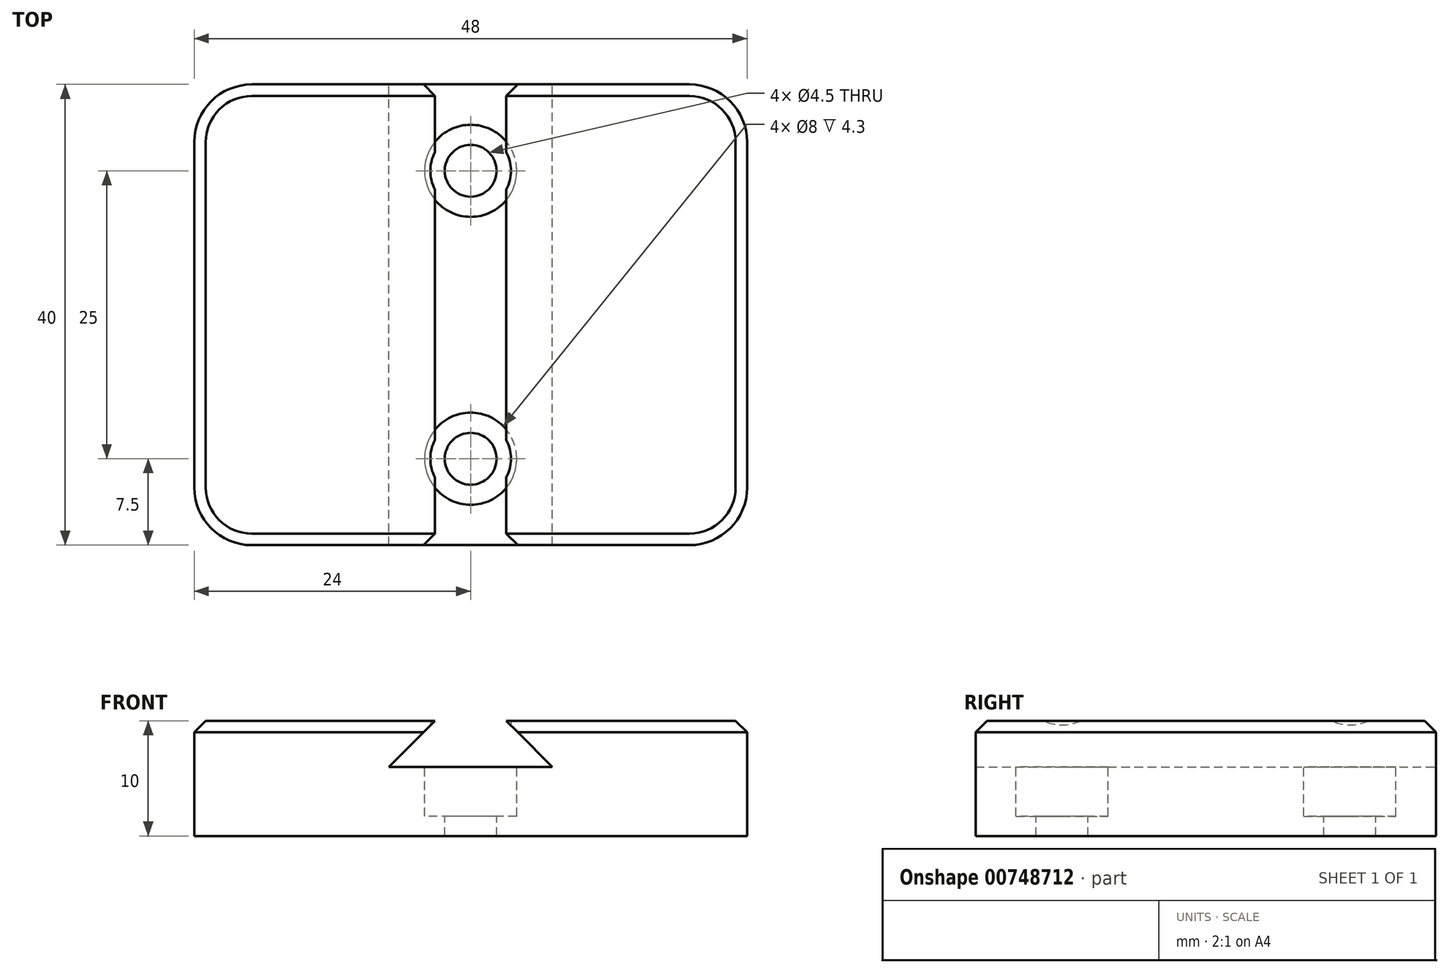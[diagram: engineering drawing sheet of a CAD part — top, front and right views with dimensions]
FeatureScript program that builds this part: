
annotation { "Feature Type Name" : "Feature", "Feature Type Description" : "" }
export const myFeature = defineFeature(function(context is Context, id is Id, definition is map)
    precondition{}
    {
        {
            var Q0;
            Q0=qCreatedBy(makeId("Front.planeOp"),FACE);
            var sketch = newSketch(context, id + "F0", { "sketchPlane" : qUnion([Q0])});
            skLineSegment(sketch, "E0", {"start": v(-24, 0) * mm, "end": v(-24, -6) * mm});
            skLineSegment(sketch, "E1", {"start": v(-24, -6) * mm, "end": v(24, -6) * mm});
            skLineSegment(sketch, "E2", {"start": v(24, -6) * mm, "end": v(24, 0) * mm});
            skLineSegment(sketch, "E3", {"start": v(-24, 0) * mm, "end": v(-24, 4) * mm});
            skLineSegment(sketch, "E4", {"start": v(-24, 4) * mm, "end": v(-3.1, 4) * mm});
            skLineSegment(sketch, "E5", {"start": v(-3.1, 4) * mm, "end": v(-7.1, 0) * mm});
            skLineSegment(sketch, "E6", {"start": v(-7.1, 0) * mm, "end": v(7.1, 0) * mm});
            skLineSegment(sketch, "E7", {"start": v(7.1, 0) * mm, "end": v(3.1, 4) * mm});
            skLineSegment(sketch, "E8", {"start": v(3.1, 4) * mm, "end": v(24, 4) * mm});
            skLineSegment(sketch, "E9", {"start": v(24, 4) * mm, "end": v(24, 0) * mm});
            skSolve(sketch);
        }
        {
            var Q0;
            Q0=makeQuery(id+"F0.imprint","IMPRINT",FACE,{"disambiguationData":[TD([[makeQuery(id+"F0.imprint","IMPRINT",EDGE,{"derivedFrom":sQuery(id+"F0.wireOp",EDGE,"E0")}),1.0]])]});
            extrude(context, id + "F1", {"entities" : qUnion([Q0]), "endBound" : BoundingType.SYMMETRIC, "depth" : 40 * mm, "offsetDistance" : 25 * mm});
        }
        {
            var Q0;
            Q0=makeQuery(id+"F1.opExtrude","CAP_EDGE",EDGE,{"disambiguationData":[OSD([sQuery(id+"F0.wireOp",EDGE,"E0"),sQuery(id+"F0.wireOp",EDGE,"E3")])],"isStart":true});
            var Q1;
            Q1=makeQuery(id+"F1.opExtrude","CAP_EDGE",EDGE,{"disambiguationData":[OSD([sQuery(id+"F0.wireOp",EDGE,"E2"),sQuery(id+"F0.wireOp",EDGE,"E9")])],"isStart":true});
            var Q2;
            Q2=makeQuery(id+"F1.opExtrude","CAP_EDGE",EDGE,{"disambiguationData":[OSD([sQuery(id+"F0.wireOp",EDGE,"E2"),sQuery(id+"F0.wireOp",EDGE,"E9")])],"isStart":false});
            var Q3;
            Q3=makeQuery(id+"F1.opExtrude","CAP_EDGE",EDGE,{"disambiguationData":[OSD([sQuery(id+"F0.wireOp",EDGE,"E0"),sQuery(id+"F0.wireOp",EDGE,"E3")])],"isStart":false});
            fillet(context, id + "F2", {"entities" : qUnion([Q0, Q1, Q2, Q3]), "radius" : 5 * mm, "tangentPropagation" : true, "allowEdgeOverflow" : false});
        }
        {
            var Q0;
            Q0=makeQuery(id+"F2.opFillet","BLEND_EDGE",EDGE,{"blendedFrom":[makeQuery(id+"F1.opExtrude","CAP_EDGE",EDGE,{"disambiguationData":[OSD([sQuery(id+"F0.wireOp",EDGE,"E0"),sQuery(id+"F0.wireOp",EDGE,"E3")])],"isStart":false}),makeQuery(id+"F1.opExtrude","SWEPT_FACE",FACE,{"disambiguationData":[OSD([sQuery(id+"F0.wireOp",EDGE,"E4")])]})],"blendedInto":[makeQuery(id+"F1.opExtrude","SWEPT_FACE",FACE,{"disambiguationData":[OSD([sQuery(id+"F0.wireOp",EDGE,"E4")])]})]});
            var Q1;
            Q1=makeQuery(id+"F1.opExtrude","CAP_EDGE",EDGE,{"disambiguationData":[OSD([sQuery(id+"F0.wireOp",EDGE,"E8")])],"isStart":false});
            chamfer(context, id + "F3", {"entities" : qUnion([Q0, Q1]), "width" : 1 * mm, "tangentPropagation" : true});
        }
        {
            var Q0;
            Q0=makeQuery(id+"F1.opExtrude","SWEPT_FACE",FACE,{"disambiguationData":[OSD([sQuery(id+"F0.wireOp",EDGE,"E6")])]});
            var sketch = newSketch(context, id + "F4", { "sketchPlane" : qUnion([Q0])});
            skPoint(sketch, "E10", {"position": v(0, 12.5) * mm});
            skPoint(sketch, "E11", {"position": v(0, -12.5) * mm});
            skCircle(sketch, "E12", {"center": v(0, -12.5) * mm, "radius": 3.5 * mm});
            skCircle(sketch, "E13", {"center": v(0, 12.5) * mm, "radius": 3.5 * mm});
            skSolve(sketch);
        }
        {
            var Q0;
            Q0=sQuery(id+"F4.wireOp",VERTEX,"E10");
            var Q1;
            Q1=sQuery(id+"F4.wireOp",VERTEX,"E11");
            var Q2;
            Q2=makeQuery(id+"F1.opExtrude","SWEPT_BODY",BODY,{"disambiguationData":[OSD([sQuery(id+"F0.wireOp",EDGE,"E0"),sQuery(id+"F0.wireOp",EDGE,"E1"),sQuery(id+"F0.wireOp",EDGE,"E2"),sQuery(id+"F0.wireOp",EDGE,"E3"),sQuery(id+"F0.wireOp",EDGE,"E4"),sQuery(id+"F0.wireOp",EDGE,"E5"),sQuery(id+"F0.wireOp",EDGE,"E6"),sQuery(id+"F0.wireOp",EDGE,"E7"),sQuery(id+"F0.wireOp",EDGE,"E8"),sQuery(id+"F0.wireOp",EDGE,"E9")])]});
            hole(context, id + "F5", {"style" : HoleStyle.C_BORE, "endStyle" : HoleEndStyle.BLIND, "holeDiameter" : 4.5 * mm, "cBoreDiameter" : 8 * mm, "cBoreDepth" : 4.3 * mm, "majorDiameter" : 5 * mm, "holeDepth" : 7 * mm, "isTappedThrough" : true, "tappedDepth" : 12 * mm, "tapClearance" : 3, "startFromSketch" : true, "locations" : qUnion([Q0, Q1]), "scope" : qUnion([Q2])});
        }
        {
            var Q0;
            Q0=makeQuery(id+"F4.imprint","IMPRINT",FACE,{"disambiguationData":[TD([[makeQuery(id+"F4.imprint","IMPRINT",EDGE,{"derivedFrom":sQuery(id+"F4.wireOp",EDGE,"E12")}),1.0]])]});
            var Q1;
            Q1=makeQuery(id+"F4.imprint","IMPRINT",FACE,{"disambiguationData":[TD([[makeQuery(id+"F4.imprint","IMPRINT",EDGE,{"derivedFrom":sQuery(id+"F4.wireOp",EDGE,"E13")}),1.0]])]});
            var Q2;
            Q2=sQuery(id+"F4.wireOp",EDGE,"E12");
            var Q3;
            Q3=sQuery(id+"F4.wireOp",EDGE,"E13");
            extrude(context, id + "F6", {"entities" : qUnion([Q0, Q1]), "operationType" : NewBodyOperationType.REMOVE, "surfaceEntities" : qUnion([Q2, Q3]), "depth" : 25 * mm, "offsetDistance" : 25 * mm});
        }
    });
